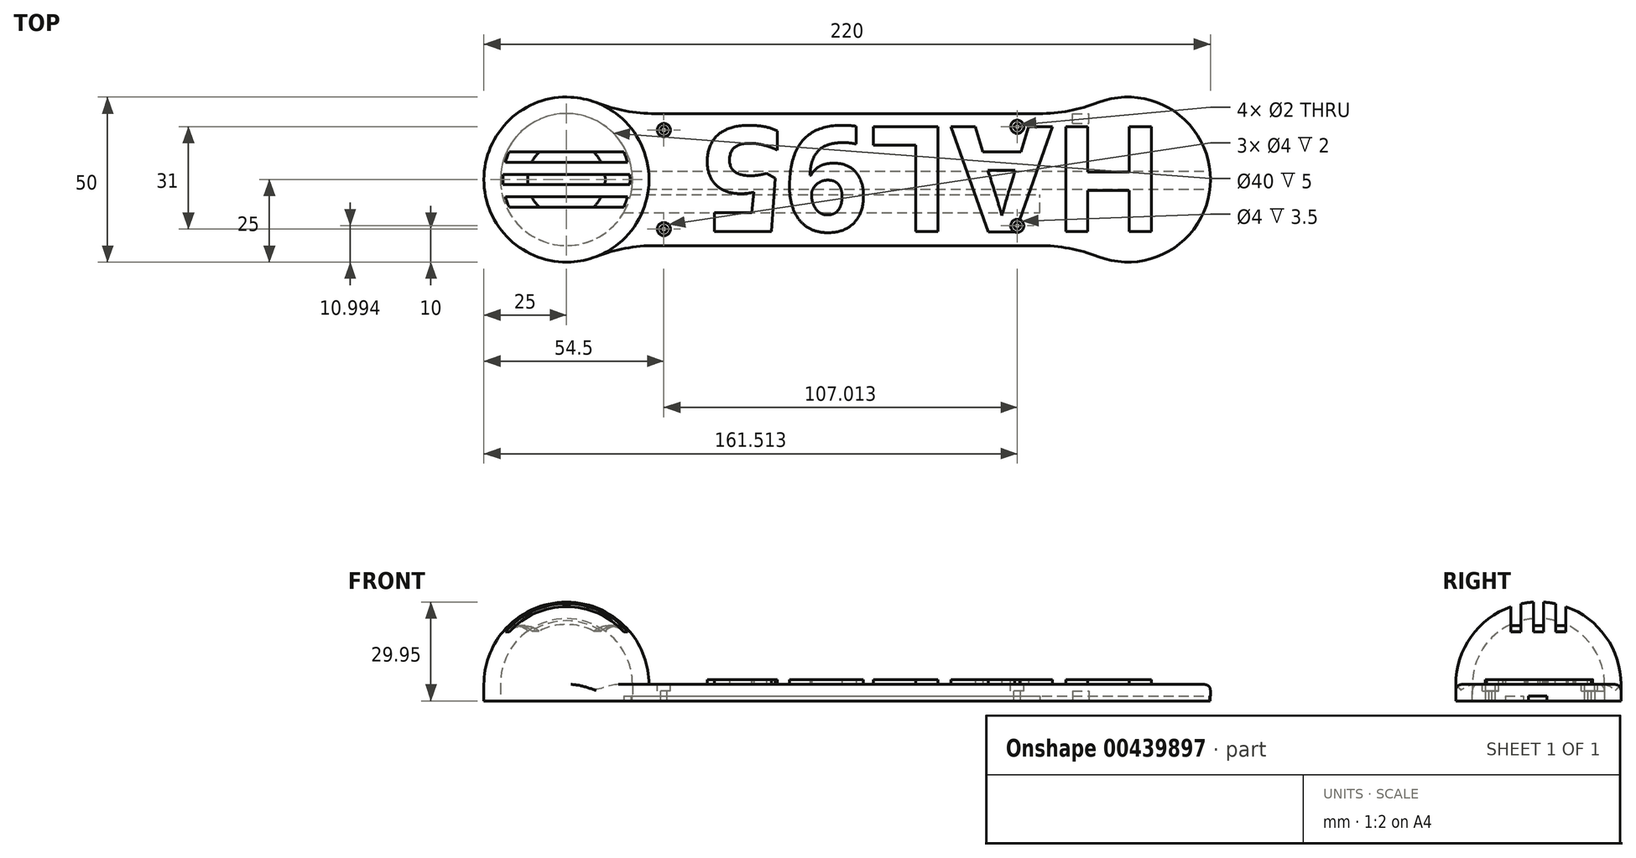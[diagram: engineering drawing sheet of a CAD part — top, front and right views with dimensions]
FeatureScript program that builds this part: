
annotation { "Feature Type Name" : "Feature", "Feature Type Description" : "" }
export const myFeature = defineFeature(function(context is Context, id is Id, definition is map)
    precondition{}
    {
        {
            var Q0;
            Q0=qCreatedBy(makeId("Top.planeOp"),FACE);
            var sketch = newSketch(context, id + "F0", { "sketchPlane" : qUnion([Q0])});
            skLineSegment(sketch, "E0.bottom", {"start": v(27, 10) * mm, "end": v(32, 10) * mm, "construction": true});
            skLineSegment(sketch, "E0.top", {"start": v(27, -10) * mm, "end": v(32, -10) * mm, "construction": true});
            skLineSegment(sketch, "E0.left", {"start": v(27, 10) * mm, "end": v(27, -10) * mm, "construction": true});
            skLineSegment(sketch, "E0.right", {"start": v(32, 10) * mm, "end": v(32, -10) * mm, "construction": true});
            skLineSegment(sketch, "E1.1.0.0", {"start": v(197, -10) * mm, "end": v(202, -10) * mm, "construction": true});
            skLineSegment(sketch, "E1.1.0.1", {"start": v(197, 10) * mm, "end": v(202, 10) * mm, "construction": true});
            skLineSegment(sketch, "E1.1.0.2", {"start": v(202, 10) * mm, "end": v(202, -10) * mm, "construction": true});
            skLineSegment(sketch, "E1.1.0.3", {"start": v(197, 10) * mm, "end": v(197, -10) * mm, "construction": true});
            skCircle(sketch, "E2.1.0.0", {"center": v(170, 0) * mm, "radius": 25 * mm});
            skLineSegment(sketch, "E3", {"start": v(15, -20) * mm, "end": v(155, -20) * mm});
            skLineSegment(sketch, "E4", {"start": v(15, 20) * mm, "end": v(155, 20) * mm});
            skLineSegment(sketch, "E5", {"start": v(254.3, 0) * mm, "end": v(-36.3, 0) * mm, "construction": true});
            skLineSegment(sketch, "E6", {"start": v(29.5, 22.1) * mm, "end": v(29.5, -23.24) * mm, "construction": true});
            skPoint(sketch, "E6.endSnap0", {"position": v(29.5, -10) * mm});
            skCircle(sketch, "E7", {"center": v(0, 0) * mm, "radius": 25 * mm});
            skCircle(sketch, "E8", {"center": v(0, 0) * mm, "radius": 20 * mm});
            skLineSegment(sketch, "E9.bottom", {"start": v(24.5, 20) * mm, "end": v(34.5, 20) * mm, "construction": true});
            skLineSegment(sketch, "E9.top", {"start": v(24.5, 10) * mm, "end": v(34.5, 10) * mm, "construction": true});
            skLineSegment(sketch, "E9.left", {"start": v(24.5, 20) * mm, "end": v(24.5, 10) * mm, "construction": true});
            skLineSegment(sketch, "E9.right", {"start": v(34.5, 20) * mm, "end": v(34.5, 10) * mm, "construction": true});
            skLineSegment(sketch, "E10.MirrorCS", {"start": v(24.5, -20) * mm, "end": v(34.5, -20) * mm, "construction": true});
            skLineSegment(sketch, "E11.MirrorCS", {"start": v(34.5, -20) * mm, "end": v(34.5, -10) * mm, "construction": true});
            skLineSegment(sketch, "E12.MirrorCS", {"start": v(24.5, -10) * mm, "end": v(34.5, -10) * mm, "construction": true});
            skLineSegment(sketch, "E13.MirrorCS", {"start": v(24.5, -20) * mm, "end": v(24.5, -10) * mm, "construction": true});
            skLineSegment(sketch, "E14.MirrorCS", {"start": v(180.7, 17) * mm, "end": v(180.7, 22) * mm, "construction": true});
            skLineSegment(sketch, "E15.MirrorCS", {"start": v(140.7, 17) * mm, "end": v(140.7, 22) * mm, "construction": true});
            skLineSegment(sketch, "E16.MirrorCS", {"start": v(140.7, 19.5) * mm, "end": v(180.7, 19.5) * mm, "construction": true});
            skLineSegment(sketch, "E17.MirrorCS", {"start": v(140.7, 22) * mm, "end": v(180.7, 22) * mm, "construction": true});
            skLineSegment(sketch, "E18.MirrorCS", {"start": v(140.7, 17) * mm, "end": v(180.7, 17) * mm, "construction": true});
            skSolve(sketch);
        }
        {
            var Q0;
            {var subQ0=sQuery(id+"F0.wireOp",EDGE,"E3");Q0=makeQuery(id+"F0.imprint","IMPRINT",FACE,{"disambiguationData":[TD([[makeQuery(id+"F0.imprint","IMPRINT",EDGE,{"derivedFrom":subQ0}),1.0]])]});}
            var Q1;
            Q1=makeQuery(id+"F0.imprint","IMPRINT",FACE,{"disambiguationData":[TD([[makeQuery(id+"F0.imprint","IMPRINT",EDGE,{"derivedFrom":sQuery(id+"F0.wireOp",EDGE,"E8")}),-1.0]])]});
            var Q2;
            {var subQ0=sQuery(id+"F0.wireOp",EDGE,"E2.1.0.0");var subQ1=makeQuery(id+"F0.imprint","INTERSECT",VERTEX,{"derivedFrom":[subQ0,sQuery(id+"F0.wireOp",EDGE,"E3")]});Q2=makeQuery(id+"F0.imprint","IMPRINT",FACE,{"disambiguationData":[TD([[makeQuery(id+"F0.imprint","IMPRINT",EDGE,{"disambiguationData":[TD([[subQ1,1.0]])],"derivedFrom":subQ0}),1.0]])]});}
            extrude(context, id + "F1", {"entities" : qUnion([Q0, Q1, Q2]), "depth" : 5 * mm});
        }
        {
            var Q0;
            Q0=makeQuery(id+"F1.opExtrude","CAP_FACE",FACE,{"disambiguationData":[OSD([sQuery(id+"F0.wireOp",EDGE,"E2.1.0.0"),sQuery(id+"F0.wireOp",EDGE,"E3"),sQuery(id+"F0.wireOp",EDGE,"E4"),sQuery(id+"F0.wireOp",EDGE,"E7"),sQuery(id+"F0.wireOp",EDGE,"E8")])],"isStart":false});
            var sketch = newSketch(context, id + "F2", { "sketchPlane" : qUnion([Q0])});
            skCircle(sketch, "E19", {"center": v(29.5, 15) * mm, "radius": 0.88 * mm, "construction": true});
            skCircle(sketch, "E20.MirrorC", {"center": v(29.5, -15) * mm, "radius": 0.88 * mm, "construction": true});
            skLineSegment(sketch, "E21", {"start": v(29.5, -15) * mm, "end": v(29.5, 15) * mm, "construction": true});
            skText(sketch, "E22", { "text": "HAL95", "fontName": "OpenSans-Bold.ttf"});
            const initialGuessF2  = {"E22": [0.18116, 0.016, -1, 0, 0.032]};
            skSetInitialGuess(sketch, initialGuessF2);
            skSolve(sketch);
        }
        {
            var Q0;
            Q0=makeQuery(id+"F1.opExtrude","CAP_FACE",FACE,{"disambiguationData":[OSD([sQuery(id+"F0.wireOp",EDGE,"E2.1.0.0"),sQuery(id+"F0.wireOp",EDGE,"E3"),sQuery(id+"F0.wireOp",EDGE,"E4"),sQuery(id+"F0.wireOp",EDGE,"E7"),sQuery(id+"F0.wireOp",EDGE,"E8")])],"isStart":false});
            var sketch = newSketch(context, id + "F3", { "sketchPlane" : qUnion([Q0])});
            skLineSegment(sketch, "E23.MirrorCS", {"start": v(140.51, 17) * mm, "end": v(140.51, 22) * mm, "construction": true});
            skLineSegment(sketch, "E24.MirrorCS", {"start": v(140.51, 17) * mm, "end": v(180.51, 17) * mm, "construction": true});
            skLineSegment(sketch, "E25.MirrorCS", {"start": v(140.51, 17) * mm, "end": v(140.51, 1.2) * mm, "construction": true});
            skLineSegment(sketch, "E26.MirrorCS", {"start": v(136.51, 19.5) * mm, "end": v(136.51, 1.2) * mm, "construction": true});
            skCircle(sketch, "E27.MirrorC", {"center": v(136.51, -14) * mm, "radius": 4 * mm, "construction": true});
            skLineSegment(sketch, "E28.MirrorCS", {"start": v(132.51, 23.4) * mm, "end": v(180.51, 23.4) * mm, "construction": true});
            skLineSegment(sketch, "E29.MirrorCS", {"start": v(132.51, 23.4) * mm, "end": v(132.51, 1.2) * mm, "construction": true});
            skLineSegment(sketch, "E30.MirrorCS", {"start": v(180.51, 17) * mm, "end": v(180.51, 23.4) * mm, "construction": true});
            skCircle(sketch, "E31.0.1.0", {"center": v(136.51, 16) * mm, "radius": 4 * mm, "construction": true});
            skSolve(sketch);
        }
        {
            var Q0;
            Q0=sQuery(id+"F2.wireOp",VERTEX,"E19.center");
            var Q1;
            Q1=sQuery(id+"F2.wireOp",VERTEX,"E20.MirrorC.center");
            var Q2;
            Q2=makeQuery(id+"F1.opExtrude","SWEPT_BODY",BODY,{"disambiguationData":[OSD([sQuery(id+"F0.wireOp",EDGE,"E2.1.0.0"),sQuery(id+"F0.wireOp",EDGE,"E3"),sQuery(id+"F0.wireOp",EDGE,"E4"),sQuery(id+"F0.wireOp",EDGE,"E7"),sQuery(id+"F0.wireOp",EDGE,"E8")])]});
            hole(context, id + "F4", {"style" : HoleStyle.C_BORE, "endStyle" : HoleEndStyle.BLIND, "holeDiameter" : 2 * mm, "cBoreDiameter" : 4 * mm, "cBoreDepth" : 2 * mm, "holeDepth" : 5 * mm, "isTappedThrough" : true, "tappedDepth" : 12 * mm, "tapClearance" : 3, "startFromSketch" : true, "locations" : qUnion([Q0, Q1]), "scope" : qUnion([Q2])});
        }
        {
            var Q0;
            Q0=qCreatedBy(makeId("Top.planeOp"),FACE);
            cPlane(context, id + "F5", {"entities" : qUnion([Q0]), "cplaneType" : CPlaneType.OFFSET, "offset" : 30 * mm, "width" : 150 * mm, "height" : 150 * mm});
        }
        {
            var Q0;
            Q0=qCreatedBy(id+"F5.planeOp",FACE);
            var sketch = newSketch(context, id + "F6", { "sketchPlane" : qUnion([Q0])});
            skCircle(sketch, "E32", {"center": v(0, 0) * mm, "radius": 11.73 * mm});
            skPoint(sketch, "E33.endSnap0", {"position": v(0, 10.2) * mm});
            skLineSegment(sketch, "E34", {"start": v(-11.63, 1.55) * mm, "end": v(11.63, 1.55) * mm});
            skLineSegment(sketch, "E35.0.1.0", {"start": v(-10.5, 5.25) * mm, "end": v(10.5, 5.25) * mm});
            skLineSegment(sketch, "E35.0.2.0", {"start": v(-8.25, 8.34) * mm, "end": v(8.25, 8.34) * mm});
            skLineSegment(sketch, "E35.0.3.0", {"start": v(-11.63, -1.54) * mm, "end": v(11.63, -1.54) * mm});
            skLineSegment(sketch, "E35.0.4.0", {"start": v(-10.5, -5.24) * mm, "end": v(10.5, -5.24) * mm});
            skLineSegment(sketch, "E35.0.5.0", {"start": v(-8.26, -8.33) * mm, "end": v(8.26, -8.33) * mm});
            skSolve(sketch);
        }
        {
            var Q0;
            Q0=makeQuery(id+"F1.opExtrude","CAP_FACE",FACE,{"disambiguationData":[OSD([sQuery(id+"F0.wireOp",EDGE,"E2.1.0.0"),sQuery(id+"F0.wireOp",EDGE,"E3"),sQuery(id+"F0.wireOp",EDGE,"E4"),sQuery(id+"F0.wireOp",EDGE,"E7"),sQuery(id+"F0.wireOp",EDGE,"E8")])],"isStart":false});
            var sketch = newSketch(context, id + "F7", { "sketchPlane" : qUnion([Q0])});
            skArc(sketch, "E36", {"start": v(20, 0) * mm, "mid": v(0, 20) * mm, "end": v(-20, 0) * mm});
            skLineSegment(sketch, "E37", {"start": v(-25, 0) * mm, "end": v(25, 0) * mm});
            skArc(sketch, "E38", {"start": v(25, 0) * mm, "mid": v(0, 25) * mm, "end": v(-25, 0) * mm});
            skSolve(sketch);
        }
        {
            var Q0;
            {var subQ4=sQuery(id+"F7.wireOp",EDGE,"E36");Q0=makeQuery(id+"F7.imprint","IMPRINT",FACE,{"disambiguationData":[TD([[makeQuery(id+"F7.imprint","IMPRINT",EDGE,{"derivedFrom":subQ4}),-1.0]])]});}
            var Q1;
            Q1=sQuery(id+"F7.wireOp",EDGE,"E37");
            revolve(context, id + "F8", {"operationType" : NewBodyOperationType.ADD, "entities" : qUnion([Q0]), "axis" : qUnion([Q1]), "revolveType" : RevolveType.ONE_DIRECTION, "angle" : 180 * degree});
        }
        {
            var Q0;
            {var subQ0=sQuery(id+"F6.wireOp",EDGE,"E35.0.1.0");Q0=makeQuery(id+"F6.imprint","IMPRINT",FACE,{"disambiguationData":[TD([[makeQuery(id+"F6.imprint","IMPRINT",EDGE,{"derivedFrom":subQ0}),1.0]])]});}
            var Q1;
            {var subQ0=sQuery(id+"F6.wireOp",EDGE,"E34");Q1=makeQuery(id+"F6.imprint","IMPRINT",FACE,{"disambiguationData":[TD([[makeQuery(id+"F6.imprint","IMPRINT",EDGE,{"derivedFrom":subQ0}),-1.0]])]});}
            var Q2;
            {var subQ0=sQuery(id+"F6.wireOp",EDGE,"E35.0.4.0");Q2=makeQuery(id+"F6.imprint","IMPRINT",FACE,{"disambiguationData":[TD([[makeQuery(id+"F6.imprint","IMPRINT",EDGE,{"derivedFrom":subQ0}),-1.0]])]});}
            extrude(context, id + "F9", {"entities" : qUnion([Q0, Q1, Q2]), "operationType" : NewBodyOperationType.REMOVE, "oppositeDirection" : true, "depth" : 25 * mm});
        }
        {
            var Q0;
            {var subQ0=sQuery(id+"F6.wireOp",EDGE,"E32");Q0=makeQuery(id+"F9.boolean.opBoolean","INTERSECT",EDGE,{"derivedFrom":[makeQuery(id+"F8.opRevolve","SWEPT_FACE",FACE,{"disambiguationData":[OSD([sQuery(id+"F7.wireOp",EDGE,"E38")])]}),makeQuery(id+"F9.opExtrude","SWEPT_FACE",FACE,{"disambiguationData":[OSD([subQ0]),TDD([makeQuery(id+"F6.imprint","IMPRINT",EDGE,{"disambiguationData":[TD([[makeQuery(id+"F6.imprint","INTERSECT",VERTEX,{"disambiguationData":[OD(0.0)],"derivedFrom":[subQ0,sQuery(id+"F6.wireOp",EDGE,"E35.0.1.0")]}),1.0]])],"derivedFrom":subQ0})])]})]});}
            var Q1;
            {var subQ0=sQuery(id+"F6.wireOp",EDGE,"E32");Q1=makeQuery(id+"F9.boolean.opBoolean","INTERSECT",EDGE,{"derivedFrom":[makeQuery(id+"F8.opRevolve","SWEPT_FACE",FACE,{"disambiguationData":[OSD([sQuery(id+"F7.wireOp",EDGE,"E38")])]}),makeQuery(id+"F9.opExtrude","SWEPT_FACE",FACE,{"disambiguationData":[OSD([subQ0]),TDD([makeQuery(id+"F6.imprint","IMPRINT",EDGE,{"disambiguationData":[TD([[makeQuery(id+"F6.imprint","INTERSECT",VERTEX,{"disambiguationData":[OD(1.0)],"derivedFrom":[subQ0,sQuery(id+"F6.wireOp",EDGE,"E35.0.1.0")]}),-1.0]])],"derivedFrom":subQ0})])]})]});}
            var Q2;
            {var subQ0=sQuery(id+"F6.wireOp",EDGE,"E32");Q2=makeQuery(id+"F9.boolean.opBoolean","INTERSECT",EDGE,{"derivedFrom":[makeQuery(id+"F8.opRevolve","SWEPT_FACE",FACE,{"disambiguationData":[OSD([sQuery(id+"F7.wireOp",EDGE,"E38")])]}),makeQuery(id+"F9.opExtrude","SWEPT_FACE",FACE,{"disambiguationData":[OSD([subQ0]),TDD([makeQuery(id+"F6.imprint","IMPRINT",EDGE,{"disambiguationData":[TD([[makeQuery(id+"F6.imprint","INTERSECT",VERTEX,{"disambiguationData":[OD(0.0)],"derivedFrom":[subQ0,sQuery(id+"F6.wireOp",EDGE,"E34")]}),-1.0]])],"derivedFrom":subQ0})])]})]});}
            var Q3;
            {var subQ0=sQuery(id+"F6.wireOp",EDGE,"E32");Q3=makeQuery(id+"F9.boolean.opBoolean","INTERSECT",EDGE,{"derivedFrom":[makeQuery(id+"F8.opRevolve","SWEPT_FACE",FACE,{"disambiguationData":[OSD([sQuery(id+"F7.wireOp",EDGE,"E38")])]}),makeQuery(id+"F9.opExtrude","SWEPT_FACE",FACE,{"disambiguationData":[OSD([subQ0]),TDD([makeQuery(id+"F6.imprint","IMPRINT",EDGE,{"disambiguationData":[TD([[makeQuery(id+"F6.imprint","INTERSECT",VERTEX,{"disambiguationData":[OD(0.0)],"derivedFrom":[subQ0,sQuery(id+"F6.wireOp",EDGE,"E35.0.4.0")]}),-1.0]])],"derivedFrom":subQ0})])]})]});}
            var Q4;
            {var subQ0=sQuery(id+"F6.wireOp",EDGE,"E32");Q4=makeQuery(id+"F9.boolean.opBoolean","INTERSECT",EDGE,{"derivedFrom":[makeQuery(id+"F8.opRevolve","SWEPT_FACE",FACE,{"disambiguationData":[OSD([sQuery(id+"F7.wireOp",EDGE,"E38")])]}),makeQuery(id+"F9.opExtrude","SWEPT_FACE",FACE,{"disambiguationData":[OSD([subQ0]),TDD([makeQuery(id+"F6.imprint","IMPRINT",EDGE,{"disambiguationData":[TD([[makeQuery(id+"F6.imprint","INTERSECT",VERTEX,{"disambiguationData":[OD(1.0)],"derivedFrom":[subQ0,sQuery(id+"F6.wireOp",EDGE,"E35.0.4.0")]}),1.0]])],"derivedFrom":subQ0})])]})]});}
            var Q5;
            {var subQ0=sQuery(id+"F6.wireOp",EDGE,"E32");Q5=makeQuery(id+"F9.boolean.opBoolean","INTERSECT",EDGE,{"derivedFrom":[makeQuery(id+"F8.opRevolve","SWEPT_FACE",FACE,{"disambiguationData":[OSD([sQuery(id+"F7.wireOp",EDGE,"E38")])]}),makeQuery(id+"F9.opExtrude","SWEPT_FACE",FACE,{"disambiguationData":[OSD([subQ0]),TDD([makeQuery(id+"F6.imprint","IMPRINT",EDGE,{"disambiguationData":[TD([[makeQuery(id+"F6.imprint","INTERSECT",VERTEX,{"disambiguationData":[OD(1.0)],"derivedFrom":[subQ0,sQuery(id+"F6.wireOp",EDGE,"E34")]}),1.0]])],"derivedFrom":subQ0})])]})]});}
            fillet(context, id + "F10", {"entities" : qUnion([Q0, Q1, Q2, Q3, Q4, Q5]), "radius" : 5 * mm, "tangentPropagation" : true, "allowEdgeOverflow" : false});
        }
        {
            var Q0;
            Q0=qSketchRegion(id+"F2",true);
            extrude(context, id + "F11", {"entities" : qUnion([Q0]), "operationType" : NewBodyOperationType.ADD, "depth" : 1.5 * mm, "offsetDistance" : 25 * mm});
        }
        {
            var Q0;
            Q0=makeQuery(id+"F1.opExtrude","SWEPT_EDGE",EDGE,{"disambiguationData":[OSD([sQuery(id+"F0.wireOp",EDGE,"E4"),sQuery(id+"F0.wireOp",EDGE,"E7")])]});
            var Q1;
            Q1=makeQuery(id+"F1.opExtrude","SWEPT_EDGE",EDGE,{"disambiguationData":[OSD([sQuery(id+"F0.wireOp",EDGE,"E3"),sQuery(id+"F0.wireOp",EDGE,"E7")])]});
            var Q2;
            Q2=makeQuery(id+"F1.opExtrude","SWEPT_EDGE",EDGE,{"disambiguationData":[OSD([sQuery(id+"F0.wireOp",EDGE,"E2.1.0.0"),sQuery(id+"F0.wireOp",EDGE,"E4")])]});
            var Q3;
            Q3=makeQuery(id+"F1.opExtrude","SWEPT_EDGE",EDGE,{"disambiguationData":[OSD([sQuery(id+"F0.wireOp",EDGE,"E2.1.0.0"),sQuery(id+"F0.wireOp",EDGE,"E3")])]});
            fillet(context, id + "F12", {"entities" : qUnion([Q0, Q1, Q2, Q3]), "radius" : 50 * mm, "tangentPropagation" : true, "allowEdgeOverflow" : false});
        }
        {
            var Q0;
            {var subQ0=sQuery(id+"F0.wireOp",EDGE,"E3");var subQ1=sQuery(id+"F0.wireOp",EDGE,"E2.1.0.0");var subQ2=sQuery(id+"F0.wireOp",EDGE,"E7");var subQ3=sQuery(id+"F0.wireOp",EDGE,"E4");Q0=makeQuery(id+"F12.opFillet","BLEND_EDGE",EDGE,{"blendedFrom":[makeQuery(id+"F1.opExtrude","SWEPT_EDGE",EDGE,{"disambiguationData":[OSD([subQ3,subQ2])]}),makeQuery(id+"F11.boolean.opBoolean","SPLIT",FACE,{"disambiguationData":[TD([makeQuery(id+"F1.opExtrude","SWEPT_FACE",FACE,{"disambiguationData":[OSD([subQ1])]})])],"derivedFrom":makeQuery(id+"F1.opExtrude","CAP_FACE",FACE,{"disambiguationData":[OSD([subQ1,subQ0,subQ3,subQ2,sQuery(id+"F0.wireOp",EDGE,"E8")])],"isStart":false})})],"blendedInto":[makeQuery(id+"F11.boolean.opBoolean","SPLIT",FACE,{"disambiguationData":[TD([makeQuery(id+"F1.opExtrude","SWEPT_FACE",FACE,{"disambiguationData":[OSD([subQ1])]})])],"derivedFrom":makeQuery(id+"F1.opExtrude","CAP_FACE",FACE,{"disambiguationData":[OSD([subQ1,subQ0,subQ3,subQ2,sQuery(id+"F0.wireOp",EDGE,"E8")])],"isStart":false})})]});}
            fillet(context, id + "F13", {"entities" : qUnion([Q0]), "radius" : 1.8 * mm, "tangentPropagation" : true, "allowEdgeOverflow" : false});
        }
        {
            var Q0;
            Q0=sQuery(id+"F3.wireOp",VERTEX,"0942e776-175e-459c-b5fa-a19fc591bb7d3.MirrorC.center");
            var Q1;
            Q1=sQuery(id+"F3.wireOp",VERTEX,"E27.MirrorC.center");
            var Q2;
            Q2=sQuery(id+"F3.wireOp",VERTEX,"E31.0.1.0.center");
            var Q3;
            Q3=makeQuery(id+"F1.opExtrude","SWEPT_BODY",BODY,{"disambiguationData":[OSD([sQuery(id+"F0.wireOp",EDGE,"E2.1.0.0"),sQuery(id+"F0.wireOp",EDGE,"E3"),sQuery(id+"F0.wireOp",EDGE,"E4"),sQuery(id+"F0.wireOp",EDGE,"E7"),sQuery(id+"F0.wireOp",EDGE,"E8")])]});
            hole(context, id + "F14", {"style" : HoleStyle.C_BORE, "endStyle" : HoleEndStyle.THROUGH, "holeDiameter" : 2 * mm, "cBoreDiameter" : 4 * mm, "cBoreDepth" : 2 * mm, "isTappedThrough" : true, "tappedDepth" : 12 * mm, "tapClearance" : 3, "startFromSketch" : true, "locations" : qUnion([Q0, Q1, Q2]), "scope" : qUnion([Q3])});
        }
        {
            var Q0;
            Q0=qCreatedBy(makeId("Top.planeOp"),FACE);
            var sketch = newSketch(context, id + "F15", { "sketchPlane" : qUnion([Q0])});
            skLineSegment(sketch, "E39", {"start": v(139.01, 17) * mm, "end": v(158.21, 17) * mm, "construction": true});
            skLineSegment(sketch, "E40", {"start": v(170, 0) * mm, "end": v(139.01, 17) * mm, "construction": true});
            skLineSegment(sketch, "E41.bottom", {"start": v(153.21, 17) * mm, "end": v(158.21, 17) * mm});
            skLineSegment(sketch, "E41.top", {"start": v(153.21, 20) * mm, "end": v(158.21, 20) * mm});
            skLineSegment(sketch, "E41.left", {"start": v(153.21, 17) * mm, "end": v(153.21, 20) * mm});
            skLineSegment(sketch, "E41.right", {"start": v(158.21, 17) * mm, "end": v(158.21, 20) * mm});
            skLineSegment(sketch, "E42", {"start": v(0, 0) * mm, "end": v(170, 0) * mm, "construction": true});
            skSolve(sketch);
        }
        {
            var Q0;
            Q0 = qSketchRegion(id + "F15", true);
            extrude(context, id + "F16", {"entities" : qUnion([Q0]), "operationType" : NewBodyOperationType.REMOVE, "depth" : 3 * mm});
        }
        {
            var Q0;
            Q0=qCreatedBy(makeId("Top.planeOp"),FACE);
            var sketch = newSketch(context, id + "F17", { "sketchPlane" : qUnion([Q0])});
            skLineSegment(sketch, "E43.bottom", {"start": v(9.34, -2.95) * mm, "end": v(199.52, -2.95) * mm});
            skLineSegment(sketch, "E43.top", {"start": v(9.34, 2.55) * mm, "end": v(199.52, 2.55) * mm});
            skLineSegment(sketch, "E43.left", {"start": v(9.34, -2.95) * mm, "end": v(9.34, 2.55) * mm});
            skLineSegment(sketch, "E43.right", {"start": v(199.52, -2.95) * mm, "end": v(199.52, 2.55) * mm});
            skLineSegment(sketch, "E44.bottom", {"start": v(9.34, -10.01) * mm, "end": v(143.33, -10.01) * mm});
            skLineSegment(sketch, "E44.top", {"start": v(9.34, -4.51) * mm, "end": v(143.33, -4.51) * mm});
            skLineSegment(sketch, "E44.left", {"start": v(9.34, -10.01) * mm, "end": v(9.34, -4.51) * mm});
            skLineSegment(sketch, "E44.right", {"start": v(143.33, -10.01) * mm, "end": v(143.33, -4.51) * mm});
            skSolve(sketch);
        }
        {
            var Q0;
            Q0=makeQuery(id+"F17.imprint","IMPRINT",FACE,{"disambiguationData":[TD([[makeQuery(id+"F17.imprint","IMPRINT",EDGE,{"derivedFrom":sQuery(id+"F17.wireOp",EDGE,"E44.bottom")}),1.0]])]});
            var Q1;
            Q1=makeQuery(id+"F17.imprint","IMPRINT",FACE,{"disambiguationData":[TD([[makeQuery(id+"F17.imprint","IMPRINT",EDGE,{"derivedFrom":sQuery(id+"F17.wireOp",EDGE,"E43.bottom")}),1.0]])]});
            extrude(context, id + "F18", {"entities" : qUnion([Q0, Q1]), "operationType" : NewBodyOperationType.REMOVE, "depth" : 1.5 * mm, "offsetDistance" : 25 * mm});
        }
        {
            var Q0;
            Q0=sQuery(id+"F3.wireOp",VERTEX,"E27.MirrorC.center");
            var Q1;
            Q1=makeQuery(id+"F1.opExtrude","SWEPT_BODY",BODY,{"disambiguationData":[OSD([sQuery(id+"F0.wireOp",EDGE,"E2.1.0.0"),sQuery(id+"F0.wireOp",EDGE,"E3"),sQuery(id+"F0.wireOp",EDGE,"E4"),sQuery(id+"F0.wireOp",EDGE,"E7"),sQuery(id+"F0.wireOp",EDGE,"E8")])]});
            hole(context, id + "F19", {"style" : HoleStyle.C_BORE, "endStyle" : HoleEndStyle.THROUGH, "oppositeDirection" : true, "holeDiameter" : 4 * mm, "cBoreDiameter" : 4 * mm, "cBoreDepth" : 2 * mm, "isTappedThrough" : true, "tappedDepth" : 12 * mm, "tapClearance" : 3, "startFromSketch" : true, "locations" : qUnion([Q0]), "scope" : qUnion([Q1])});
        }
    });
